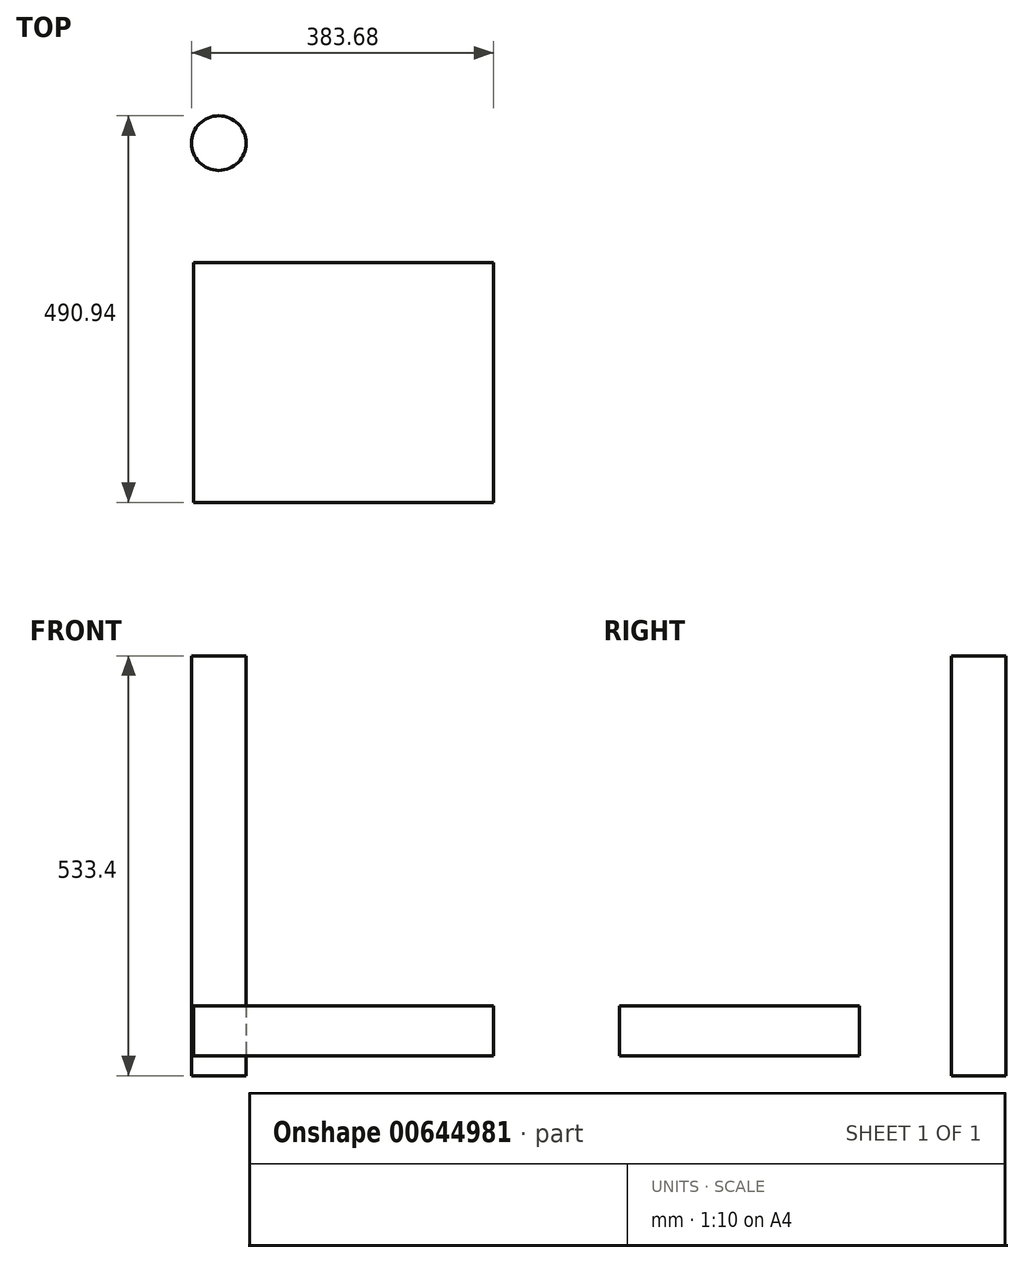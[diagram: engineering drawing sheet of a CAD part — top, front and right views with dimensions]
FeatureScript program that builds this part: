
annotation { "Feature Type Name" : "Feature", "Feature Type Description" : "" }
export const myFeature = defineFeature(function(context is Context, id is Id, definition is map)
    precondition{}
    {
        {
            var Q0;
            Q0=qCreatedBy(makeId("Front.planeOp"),FACE);
            var sketch = newSketch(context, id + "F0", { "sketchPlane" : qUnion([Q0])});
            skLineSegment(sketch, "E0", {"start": v(0, 0) * mm, "end": v(381, 0) * mm});
            skLineSegment(sketch, "E1", {"start": v(381, 63.5) * mm, "end": v(381, 0) * mm});
            skLineSegment(sketch, "E2", {"start": v(381, 63.5) * mm, "end": v(0, 63.5) * mm});
            skLineSegment(sketch, "E3", {"start": v(0, 63.5) * mm, "end": v(0, 0) * mm});
            skSolve(sketch);
        }
        {
            var Q0;
            Q0=makeQuery(id+"F0.imprint","IMPRINT",FACE,{"disambiguationData":[TD([[makeQuery(id+"F0.imprint","IMPRINT",EDGE,{"derivedFrom":sQuery(id+"F0.wireOp",EDGE,"E0")}),1.0]])]});
            extrude(context, id + "F1", {"entities" : qUnion([Q0]), "depth" : 304.8 * mm, "offsetDistance" : 25.4 * mm});
        }
        {
            var Q0;
            Q0=qCreatedBy(makeId("Top.planeOp"),FACE);
            var sketch = newSketch(context, id + "F2", { "sketchPlane" : qUnion([Q0])});
            skCircle(sketch, "E4", {"center": v(31.99, 151.47) * mm, "radius": 34.67 * mm});
            skSolve(sketch);
        }
        {
            var Q0;
            Q0 = qSketchRegion(id + "F2", true);
            extrude(context, id + "F3", {"entities" : qUnion([Q0]), "depth" : 508 * mm, "offsetDistance" : 25.4 * mm, "hasSecondDirection" : true, "secondDirectionOppositeDirection" : true, "secondDirectionDepth" : 25.4 * mm});
        }
    });
